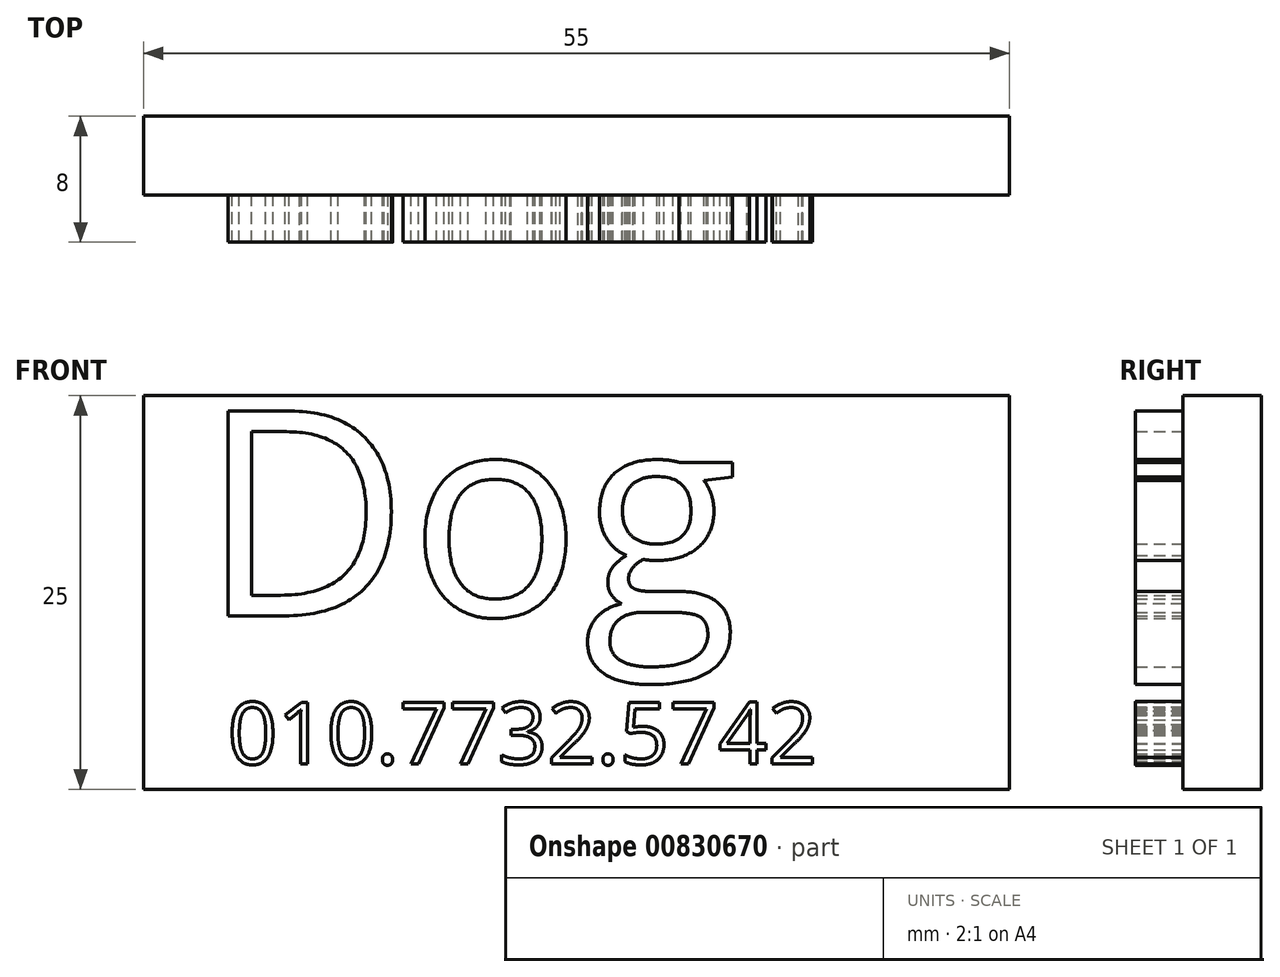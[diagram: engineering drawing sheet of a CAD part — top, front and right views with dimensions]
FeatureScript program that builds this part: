
annotation { "Feature Type Name" : "Feature", "Feature Type Description" : "" }
export const myFeature = defineFeature(function(context is Context, id is Id, definition is map)
    precondition{}
    {
        {
            var Q0;
            Q0=qCreatedBy(makeId("Front.planeOp"),FACE);
            var sketch = newSketch(context, id + "F0", { "sketchPlane" : qUnion([Q0])});
            skLineSegment(sketch, "E0.bottom", {"start": v(0, 0) * mm, "end": v(55, 0) * mm});
            skLineSegment(sketch, "E0.top", {"start": v(0, 25) * mm, "end": v(55, 25) * mm});
            skLineSegment(sketch, "E0.left", {"start": v(0, 0) * mm, "end": v(0, 25) * mm});
            skLineSegment(sketch, "E0.right", {"start": v(55, 0) * mm, "end": v(55, 25) * mm});
            skSolve(sketch);
        }
        {
            var Q0;
            Q0 = qSketchRegion(id + "F0", true);
            extrude(context, id + "F1", {"entities" : qUnion([Q0]), "depth" : 5 * mm, "offsetDistance" : 25 * mm});
        }
        {
            var Q0;
            Q0=makeQuery(id+"F1.opExtrude","CAP_FACE",FACE,{"disambiguationData":[OSD([sQuery(id+"F0.wireOp",EDGE,"E0.bottom"),sQuery(id+"F0.wireOp",EDGE,"E0.top"),sQuery(id+"F0.wireOp",EDGE,"E0.left"),sQuery(id+"F0.wireOp",EDGE,"E0.right")])],"isStart":false});
            var sketch = newSketch(context, id + "F2", { "sketchPlane" : qUnion([Q0])});
            skText(sketch, "E1", { "text": "Dog", "fontName": "OpenSans-Regular.ttf"});
            const initialGuessF2  = {"E1": [0.00357, 0.01102, 1, 0, 0.01311]};
            skSetInitialGuess(sketch, initialGuessF2);
            skSolve(sketch);
        }
        {
            var Q0;
            Q0 = qSketchRegion(id + "F2", true);
            extrude(context, id + "F3", {"entities" : qUnion([Q0]), "operationType" : NewBodyOperationType.ADD, "depth" : 3 * mm, "offsetDistance" : 25 * mm});
        }
        {
            var Q0;
            {var subQ0=sQuery(id+"F0.wireOp",EDGE,"E0.left");var subQ1=sQuery(id+"F0.wireOp",EDGE,"E0.bottom");var subQ2=sQuery(id+"F0.wireOp",EDGE,"E0.right");var subQ3=sQuery(id+"F0.wireOp",EDGE,"E0.top");Q0=makeQuery(id+"F3.boolean.opBoolean","SPLIT",FACE,{"disambiguationData":[TD([makeQuery(id+"F1.opExtrude","SWEPT_FACE",FACE,{"disambiguationData":[OSD([subQ1])]})])],"derivedFrom":makeQuery(id+"F1.opExtrude","CAP_FACE",FACE,{"disambiguationData":[OSD([subQ1,subQ3,subQ0,subQ2])],"isStart":false})});}
            var sketch = newSketch(context, id + "F4", { "sketchPlane" : qUnion([Q0])});
            skText(sketch, "E2", { "text": "010.7732.5742", "fontName": "OpenSans-Regular.ttf"});
            skPoint(sketch, "E2.firstSnap0", {"position": v(5.35, 17.52) * mm});
            const initialGuessF4  = {"E2": [0.00535, 0.0016, 1, 0, 0.00395]};
            skSetInitialGuess(sketch, initialGuessF4);
            skSolve(sketch);
        }
        {
            var Q0;
            Q0 = qSketchRegion(id + "F4", true);
            extrude(context, id + "F5", {"entities" : qUnion([Q0]), "operationType" : NewBodyOperationType.ADD, "depth" : 3 * mm, "offsetDistance" : 25 * mm});
        }
    });
